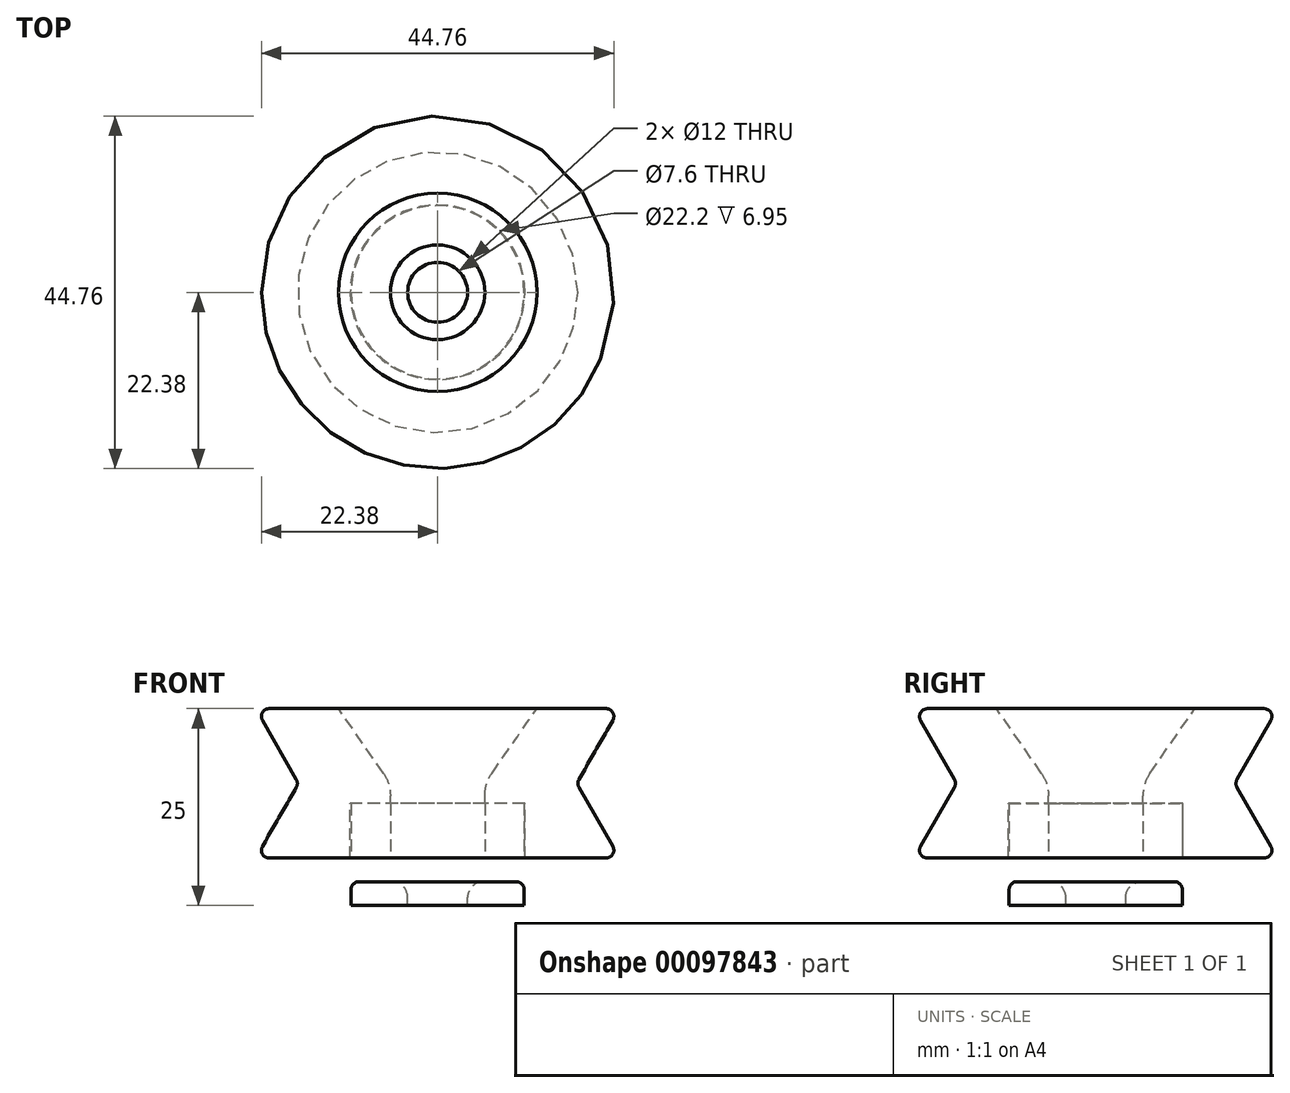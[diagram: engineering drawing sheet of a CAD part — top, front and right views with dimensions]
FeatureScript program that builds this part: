
annotation { "Feature Type Name" : "Feature", "Feature Type Description" : "" }
export const myFeature = defineFeature(function(context is Context, id is Id, definition is map)
    precondition{}
    {
        {
            var Q0;
            Q0=qCreatedBy(makeId("Top.planeOp"),FACE);
            var sketch = newSketch(context, id + "F0", { "sketchPlane" : qUnion([Q0])});
            skCircle(sketch, "E0", {"center": v(0, 0) * mm, "radius": 11 * mm});
            skCircle(sketch, "E1", {"center": v(0, 0) * mm, "radius": 3.8 * mm});
            skCircle(sketch, "E2", {"center": v(0, 0) * mm, "radius": 17.5 * mm});
            skCircle(sketch, "E3", {"center": v(0, 0) * mm, "radius": 2 * mm});
            skCircle(sketch, "E4", {"center": v(0, 0) * mm, "radius": 6 * mm});
            skCircle(sketch, "E5", {"center": v(0, 0) * mm, "radius": 14 * mm});
            skCircle(sketch, "E6", {"center": v(0, 0) * mm, "radius": 5 * mm});
            skSolve(sketch);
        }
        {
            var Q0;
            Q0=makeQuery(id+"F0.imprint","IMPRINT",FACE,{"disambiguationData":[TD([[makeQuery(id+"F0.imprint","IMPRINT",EDGE,{"derivedFrom":sQuery(id+"F0.wireOp",EDGE,"E1")}),-1.0]])]});
            var Q1;
            Q1=makeQuery(id+"F0.imprint","IMPRINT",FACE,{"disambiguationData":[TD([[makeQuery(id+"F0.imprint","IMPRINT",EDGE,{"derivedFrom":sQuery(id+"F0.wireOp",EDGE,"E0")}),1.0]])]});
            extrude(context, id + "F1", {"entities" : qUnion([Q0, Q1]), "depth" : 6.95 * mm});
        }
        {
            var Q0;
            Q0=makeQuery(id+"F0.imprint","IMPRINT",FACE,{"disambiguationData":[TD([[makeQuery(id+"F0.imprint","IMPRINT",EDGE,{"derivedFrom":sQuery(id+"F0.wireOp",EDGE,"E1")}),-1.0]])]});
            var Q1;
            Q1=makeQuery(id+"F0.imprint","IMPRINT",FACE,{"disambiguationData":[TD([[makeQuery(id+"F0.imprint","IMPRINT",EDGE,{"derivedFrom":sQuery(id+"F0.wireOp",EDGE,"E1")}),1.0]])]});
            var Q2;
            Q2=makeQuery(id+"F0.imprint","IMPRINT",FACE,{"disambiguationData":[TD([[makeQuery(id+"F0.imprint","IMPRINT",EDGE,{"derivedFrom":sQuery(id+"F0.wireOp",EDGE,"E4")}),1.0]])]});
            extrude(context, id + "F2", {"entities" : qUnion([Q0, Q1, Q2]), "oppositeDirection" : true, "depth" : 3 * mm});
        }
        {
            var Q0;
            Q0=qCreatedBy(makeId("Front.planeOp"),FACE);
            var sketch = newSketch(context, id + "F3", { "sketchPlane" : qUnion([Q0])});
            skLineSegment(sketch, "E7", {"start": v(-23.1, 0) * mm, "end": v(-17.66, 9.5) * mm});
            skLineSegment(sketch, "E8", {"start": v(-17.66, 9.5) * mm, "end": v(-23.1, 19) * mm});
            skLineSegment(sketch, "E9", {"start": v(-23.1, 0) * mm, "end": v(-11.1, 0) * mm});
            skLineSegment(sketch, "E10", {"start": v(-23.1, 19) * mm, "end": v(-12.6, 19) * mm});
            skLineSegment(sketch, "E11", {"start": v(-11.1, 0) * mm, "end": v(-11.1, 6.95) * mm});
            skLineSegment(sketch, "E12", {"start": v(-11.1, 6.95) * mm, "end": v(-6, 6.95) * mm});
            skLineSegment(sketch, "E13", {"start": v(-6, 6.95) * mm, "end": v(-6, 9.5) * mm});
            skLineSegment(sketch, "E14", {"start": v(-6, 19) * mm, "end": v(0, 19) * mm, "construction": true});
            skLineSegment(sketch, "E15", {"start": v(-17.66, 19) * mm, "end": v(-17.66, 0) * mm, "construction": true});
            skLineSegment(sketch, "E16", {"start": v(0, 19) * mm, "end": v(0, 0) * mm, "construction": true});
            skLineSegment(sketch, "E17", {"start": v(-12.6, 19) * mm, "end": v(-6, 9.5) * mm});
            skSolve(sketch);
        }
        {
            var Q0;
            Q0=makeQuery(id+"F3.imprint","IMPRINT",FACE,{"disambiguationData":[TD([[makeQuery(id+"F3.imprint","IMPRINT",EDGE,{"derivedFrom":sQuery(id+"F3.wireOp",EDGE,"E7")}),-1.0]])]});
            var Q1;
            Q1=sQuery(id+"F3.wireOp",EDGE,"E16");
            revolve(context, id + "F4", {"entities" : qUnion([Q0]), "axis" : qUnion([Q1]), "revolveType" : RevolveType.FULL});
        }
        {
            var Q0;
            Q0=makeQuery(id+"F0.imprint","IMPRINT",FACE,{"disambiguationData":[TD([[makeQuery(id+"F0.imprint","IMPRINT",EDGE,{"derivedFrom":sQuery(id+"F0.wireOp",EDGE,"E0")}),1.0]])]});
            var Q1;
            Q1=makeQuery(id+"F0.imprint","IMPRINT",FACE,{"disambiguationData":[TD([[makeQuery(id+"F0.imprint","IMPRINT",EDGE,{"derivedFrom":sQuery(id+"F0.wireOp",EDGE,"E1")}),-1.0]])]});
            var Q2;
            Q2=makeQuery(id+"F0.imprint","IMPRINT",FACE,{"disambiguationData":[TD([[makeQuery(id+"F0.imprint","IMPRINT",EDGE,{"derivedFrom":sQuery(id+"F0.wireOp",EDGE,"E4")}),1.0]])]});
            extrude(context, id + "F5", {"entities" : qUnion([Q0, Q1, Q2]), "oppositeDirection" : true, "depth" : 6 * mm, "hasSecondDirection" : true, "secondDirectionOppositeDirection" : true, "secondDirectionDepth" : 3 * mm});
        }
        {
            var Q0;
            Q0=makeQuery(id+"F4.opRevolve","SWEPT_EDGE",EDGE,{"disambiguationData":[OSD([sQuery(id+"F3.wireOp",EDGE,"E8"),sQuery(id+"F3.wireOp",EDGE,"E10")])]});
            var Q1;
            Q1=makeQuery(id+"F4.opRevolve","SWEPT_EDGE",EDGE,{"disambiguationData":[OSD([sQuery(id+"F3.wireOp",EDGE,"E7"),sQuery(id+"F3.wireOp",EDGE,"E9")])]});
            var Q2;
            Q2=makeQuery(id+"F4.opRevolve","SWEPT_EDGE",EDGE,{"disambiguationData":[OSD([sQuery(id+"F3.wireOp",EDGE,"E7"),sQuery(id+"F3.wireOp",EDGE,"E8")])]});
            var Q3;
            Q3=makeQuery(id+"F5.opExtrude","CAP_EDGE",EDGE,{"disambiguationData":[OSD([sQuery(id+"F0.wireOp",EDGE,"E0")])],"isStart":true});
            fillet(context, id + "F6", {"entities" : qUnion([Q0, Q1, Q2, Q3]), "radius" : 1 * mm, "tangentPropagation" : true, "allowEdgeOverflow" : false});
        }
        {
            var Q0;
            Q0=makeQuery(id+"F0.imprint","IMPRINT",FACE,{"disambiguationData":[TD([[makeQuery(id+"F0.imprint","IMPRINT",EDGE,{"derivedFrom":sQuery(id+"F0.wireOp",EDGE,"E1")}),-1.0]])]});
            var Q1;
            Q1=makeQuery(id+"F0.imprint","IMPRINT",FACE,{"disambiguationData":[TD([[makeQuery(id+"F0.imprint","IMPRINT",EDGE,{"derivedFrom":sQuery(id+"F0.wireOp",EDGE,"E1")}),1.0]])]});
            var Q2;
            Q2=makeQuery(id+"F1.opExtrude","CAP_FACE",FACE,{"disambiguationData":[OSD([sQuery(id+"F0.wireOp",EDGE,"E0"),sQuery(id+"F0.wireOp",EDGE,"E1")])],"isStart":false});
            extrude(context, id + "F7", {"entities" : qUnion([Q0, Q1]), "depth" : 15 * mm, "hasSecondDirection" : true, "secondDirectionBound" : SecondDirectionBoundingType.UP_TO_SURFACE, "secondDirectionOppositeDirection" : false, "secondDirectionBoundEntityFace" : qUnion([Q2]), "secondDirectionDepth" : 9.2 * mm});
        }
        {
            var Q0;
            Q0=makeQuery(id+"F0.imprint","IMPRINT",FACE,{"disambiguationData":[TD([[makeQuery(id+"F0.imprint","IMPRINT",EDGE,{"derivedFrom":sQuery(id+"F0.wireOp",EDGE,"E1")}),1.0]])]});
            var Q1;
            Q1=makeQuery(id+"F7.opExtrude","CAP_FACE",FACE,{"disambiguationData":[OSD([sQuery(id+"F0.wireOp",EDGE,"E3"),sQuery(id+"F0.wireOp",EDGE,"E4")])],"isStart":true});
            extrude(context, id + "F8", {"entities" : qUnion([Q0]), "operationType" : NewBodyOperationType.ADD, "endBound" : BoundingType.UP_TO_SURFACE, "endBoundEntityFace" : qUnion([Q1]), "depth" : 10 * mm});
        }
        {
            var Q0;
            Q0=makeQuery(id+"F7.opExtrude","CAP_EDGE",EDGE,{"disambiguationData":[OSD([sQuery(id+"F0.wireOp",EDGE,"E3")])],"isStart":false});
            chamfer(context, id + "F9", {"entities" : qUnion([Q0]), "width" : 2 * mm, "tangentPropagation" : true});
        }
        {
            var Q0;
            Q0=makeQuery(id+"F5.opExtrude","CAP_EDGE",EDGE,{"disambiguationData":[OSD([sQuery(id+"F0.wireOp",EDGE,"E1")])],"isStart":true});
            fillet(context, id + "F10", {"entities" : qUnion([Q0]), "radius" : 2 * mm, "tangentPropagation" : true, "allowEdgeOverflow" : false});
        }
        {
            var Q0;
            Q0=makeQuery(id+"F1.opExtrude","SWEPT_BODY",BODY,{"disambiguationData":[OSD([sQuery(id+"F0.wireOp",EDGE,"E1"),sQuery(id+"F0.wireOp",EDGE,"E6")])]});
            deleteBodies(context, id + "F11", {"entities" : qUnion([Q0])});
        }
        {
            var Q0;
            Q0=makeQuery(id+"F4.opRevolve","SWEPT_EDGE",EDGE,{"disambiguationData":[OSD([sQuery(id+"F3.wireOp",EDGE,"E13"),sQuery(id+"F3.wireOp",EDGE,"E17")])]});
            fillet(context, id + "F12", {"entities" : qUnion([Q0]), "radius" : 5 * mm, "tangentPropagation" : true, "allowEdgeOverflow" : false});
        }
    });
